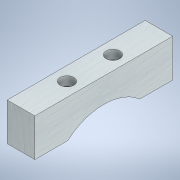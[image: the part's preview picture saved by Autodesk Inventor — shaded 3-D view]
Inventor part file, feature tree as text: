
AUTODESK INVENTOR PART (.ipt)
format: ipt  version: 2022.4 (Build 264492010, 492A)  size: 140,800 bytes
history: native  units: mm
features: extrude x3, sketch x3, other x1
ambient origin geometry x8: Origin, YZ Plane, XZ Plane, XY Plane, X Axis, Y Axis, Z Axis, Center Point
bodies: Body1 (feature_tree)
feature tree (7):
  other  "Sólido1"
  extrude  "Extrusión1"  Depth=20.0mm
  extrude  "Extrusión2"  Depth=66.666667mm
  extrude  "Extrusión3"  Depth=40.0mm
  sketch  "Boceto1"  dims[d3=0.0mm d4=20.0mm]
  sketch  "Boceto2"  dims[d5=20.0mm d7=66.666667mm]
  sketch  "Boceto3"  dims[d8=20.0mm d9=20.0mm d10=13.333333mm d11=0.0mm d14=100.0mm d15=40.0mm d16=0.0mm]
